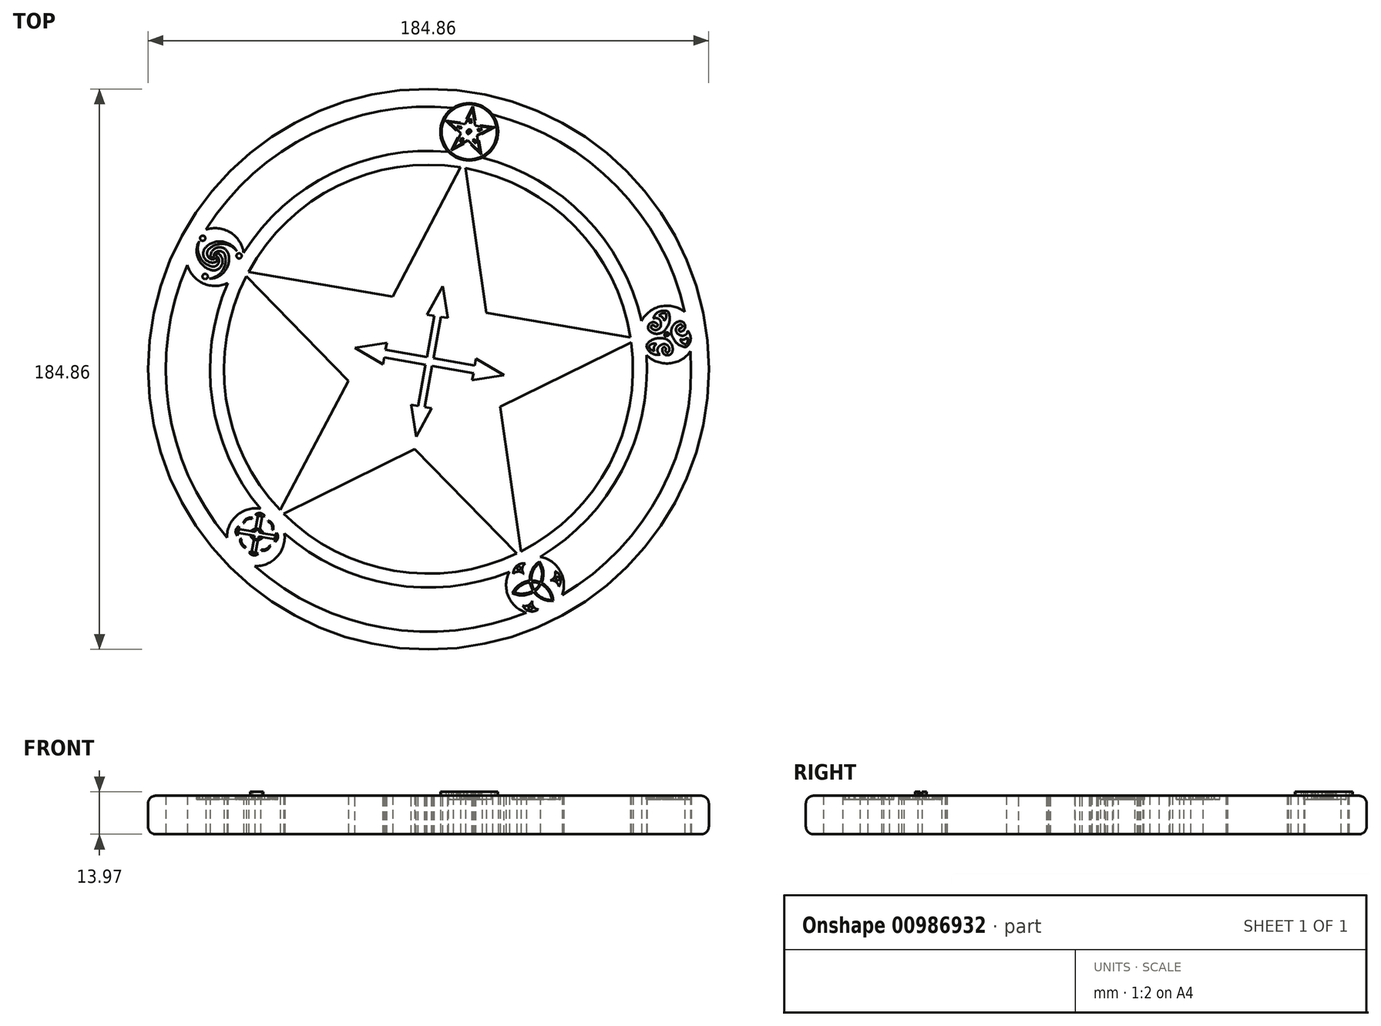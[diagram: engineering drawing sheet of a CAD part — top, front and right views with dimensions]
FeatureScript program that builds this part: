
annotation { "Feature Type Name" : "Feature", "Feature Type Description" : "" }
export const myFeature = defineFeature(function(context is Context, id is Id, definition is map)
    precondition{}
    {
        {
            var Q0;
            Q0=qCreatedBy(makeId("Top.planeOp"),FACE);
            var sketch = newSketch(context, id + "F0", { "sketchPlane" : qUnion([Q0])});
            skCircle(sketch, "E0.cCircle", {"center": v(-145.8, 0) * mm, "radius": 21.6 * mm, "construction": true});
            skLineSegment(sketch, "E0.0", {"start": v(-122.17, -12.44) * mm, "end": v(-150.33, -26.32) * mm});
            skLineSegment(sketch, "E0.1", {"start": v(-150.33, -26.32) * mm, "end": v(-172.24, -3.83) * mm});
            skLineSegment(sketch, "E0.2", {"start": v(-172.24, -3.83) * mm, "end": v(-157.62, 23.95) * mm});
            skLineSegment(sketch, "E0.3", {"start": v(-157.62, 23.95) * mm, "end": v(-126.68, 18.64) * mm});
            skLineSegment(sketch, "E0.4", {"start": v(-126.68, 18.64) * mm, "end": v(-122.17, -12.44) * mm});
            skPoint(sketch, "E0.0.midPoint", {"position": v(-136.25, -19.38) * mm});
            skLineSegment(sketch, "E1", {"start": v(-150.33, -26.32) * mm, "end": v(-195.9, -48.79) * mm});
            skLineSegment(sketch, "E2", {"start": v(-195.9, -48.79) * mm, "end": v(-172.24, -3.83) * mm});
            skLineSegment(sketch, "E3", {"start": v(-150.33, -26.32) * mm, "end": v(-114.88, -62.7) * mm});
            skLineSegment(sketch, "E4", {"start": v(-114.88, -62.7) * mm, "end": v(-122.17, -12.44) * mm});
            skLineSegment(sketch, "E5", {"start": v(-122.17, -12.44) * mm, "end": v(-76.61, 10.03) * mm});
            skLineSegment(sketch, "E6", {"start": v(-76.61, 10.03) * mm, "end": v(-126.68, 18.64) * mm});
            skLineSegment(sketch, "E7", {"start": v(-126.68, 18.64) * mm, "end": v(-133.97, 68.91) * mm});
            skLineSegment(sketch, "E8", {"start": v(-133.97, 68.91) * mm, "end": v(-157.62, 23.95) * mm});
            skLineSegment(sketch, "E9", {"start": v(-157.62, 23.95) * mm, "end": v(-207.69, 32.56) * mm});
            skLineSegment(sketch, "E10", {"start": v(-207.69, 32.56) * mm, "end": v(-172.24, -3.83) * mm});
            skCircle(sketch, "E11", {"center": v(-145.8, 0) * mm, "radius": 69.92 * mm});
            skCircle(sketch, "E12", {"center": v(-132.35, 78.3) * mm, "radius": 9.53 * mm});
            skCircle(sketch, "E13", {"center": v(-67.18, 11.4) * mm, "radius": 9.53 * mm});
            skCircle(sketch, "E14", {"center": v(-110.67, -71.25) * mm, "radius": 9.53 * mm});
            skCircle(sketch, "E15", {"center": v(-202.71, -55.44) * mm, "radius": 9.53 * mm});
            skCircle(sketch, "E16", {"center": v(-216.12, 37) * mm, "radius": 9.53 * mm});
            skCircle(sketch, "E17", {"center": v(-145.8, 0) * mm, "radius": 88.97 * mm});
            skCircle(sketch, "E18", {"center": v(-145.8, 0) * mm, "radius": 67.43 * mm});
            skCircle(sketch, "E19", {"center": v(-145.8, 0) * mm, "radius": 92.43 * mm});
            skCircle(sketch, "E20", {"center": v(-145.8, 0) * mm, "radius": 72.01 * mm});
            skCircle(sketch, "E21", {"center": v(-145.8, 0) * mm, "radius": 86.59 * mm});
            skSolve(sketch);
        }
        {
            var Q0;
            Q0 = qSketchRegion(id + "F0", true);
            var Q1;
            {var subQ0=sQuery(id+"F0.wireOp",EDGE,"E0.3");Q1=makeQuery(id+"F0.imprint","IMPRINT",FACE,{"disambiguationData":[TD([[makeQuery(id+"F0.imprint","IMPRINT",EDGE,{"derivedFrom":subQ0}),1.0]])]});}
            var Q2;
            Q2=makeQuery(id+"F0.imprint","IMPRINT",FACE,{"disambiguationData":[TD([[makeQuery(id+"F0.imprint","IMPRINT",EDGE,{"derivedFrom":sQuery(id+"F0.wireOp",EDGE,"E0.0")}),-1.0]])]});
            var Q3;
            {var subQ0=sQuery(id+"F0.wireOp",EDGE,"E0.2");Q3=makeQuery(id+"F0.imprint","IMPRINT",FACE,{"disambiguationData":[TD([[makeQuery(id+"F0.imprint","IMPRINT",EDGE,{"derivedFrom":subQ0}),1.0]])]});}
            var Q4;
            {var subQ0=sQuery(id+"F0.wireOp",EDGE,"E0.4");Q4=makeQuery(id+"F0.imprint","IMPRINT",FACE,{"disambiguationData":[TD([[makeQuery(id+"F0.imprint","IMPRINT",EDGE,{"derivedFrom":subQ0}),1.0]])]});}
            var Q5;
            {var subQ0=sQuery(id+"F0.wireOp",EDGE,"E0.0");Q5=makeQuery(id+"F0.imprint","IMPRINT",FACE,{"disambiguationData":[TD([[makeQuery(id+"F0.imprint","IMPRINT",EDGE,{"derivedFrom":subQ0}),1.0]])]});}
            var Q6;
            {var subQ1=sQuery(id+"F0.wireOp",EDGE,"E8");var subQ3=sQuery(id+"F0.wireOp",EDGE,"E18");var subQ4=makeQuery(id+"F0.imprint","INTERSECT",VERTEX,{"derivedFrom":[subQ1,subQ3]});Q6=makeQuery(id+"F0.imprint","IMPRINT",FACE,{"disambiguationData":[TD([[makeQuery(id+"F0.imprint","IMPRINT",EDGE,{"disambiguationData":[TD([[subQ4,-1.0]])],"derivedFrom":subQ3}),-1.0]])]});}
            var Q7;
            {var subQ0=sQuery(id+"F0.wireOp",EDGE,"E12");var subQ5=sQuery(id+"F0.wireOp",EDGE,"E20");var subQ6=makeQuery(id+"F0.imprint","INTERSECT",VERTEX,{"disambiguationData":[OD(0.0)],"derivedFrom":[subQ0,subQ5]});Q7=makeQuery(id+"F0.imprint","IMPRINT",FACE,{"disambiguationData":[TD([[makeQuery(id+"F0.imprint","IMPRINT",EDGE,{"disambiguationData":[TD([[subQ6,-1.0]])],"derivedFrom":subQ5}),1.0]])]});}
            var Q8;
            {var subQ1=sQuery(id+"F0.wireOp",EDGE,"E9");var subQ3=sQuery(id+"F0.wireOp",EDGE,"E18");var subQ4=makeQuery(id+"F0.imprint","INTERSECT",VERTEX,{"derivedFrom":[subQ1,subQ3]});Q8=makeQuery(id+"F0.imprint","IMPRINT",FACE,{"disambiguationData":[TD([[makeQuery(id+"F0.imprint","IMPRINT",EDGE,{"disambiguationData":[TD([[subQ4,-1.0]])],"derivedFrom":subQ3}),-1.0]])]});}
            var Q9;
            {var subQ1=sQuery(id+"F0.wireOp",EDGE,"E2");var subQ3=sQuery(id+"F0.wireOp",EDGE,"E18");var subQ4=makeQuery(id+"F0.imprint","INTERSECT",VERTEX,{"derivedFrom":[subQ1,subQ3]});Q9=makeQuery(id+"F0.imprint","IMPRINT",FACE,{"disambiguationData":[TD([[makeQuery(id+"F0.imprint","IMPRINT",EDGE,{"disambiguationData":[TD([[subQ4,1.0]])],"derivedFrom":subQ3}),-1.0]])]});}
            var Q10;
            {var subQ0=sQuery(id+"F0.wireOp",EDGE,"E16");var subQ2=sQuery(id+"F0.wireOp",EDGE,"E20");var subQ4=makeQuery(id+"F0.imprint","INTERSECT",VERTEX,{"disambiguationData":[OD(0.0)],"derivedFrom":[subQ0,subQ2]});Q10=makeQuery(id+"F0.imprint","IMPRINT",FACE,{"disambiguationData":[TD([[makeQuery(id+"F0.imprint","IMPRINT",EDGE,{"disambiguationData":[TD([[subQ4,-1.0]])],"derivedFrom":subQ2}),1.0]])]});}
            var Q11;
            {var subQ0=sQuery(id+"F0.wireOp",EDGE,"E15");var subQ5=sQuery(id+"F0.wireOp",EDGE,"E20");var subQ6=makeQuery(id+"F0.imprint","INTERSECT",VERTEX,{"disambiguationData":[OD(1.0)],"derivedFrom":[subQ0,subQ5]});Q11=makeQuery(id+"F0.imprint","IMPRINT",FACE,{"disambiguationData":[TD([[makeQuery(id+"F0.imprint","IMPRINT",EDGE,{"disambiguationData":[TD([[subQ6,1.0]])],"derivedFrom":subQ5}),1.0]])]});}
            var Q12;
            {var subQ0=sQuery(id+"F0.wireOp",EDGE,"E21");var subQ1=sQuery(id+"F0.wireOp",EDGE,"E16");var subQ2=makeQuery(id+"F0.imprint","INTERSECT",VERTEX,{"disambiguationData":[OD(0.0)],"derivedFrom":[subQ1,subQ0]});Q12=makeQuery(id+"F0.imprint","IMPRINT",FACE,{"disambiguationData":[TD([[makeQuery(id+"F0.imprint","IMPRINT",EDGE,{"disambiguationData":[TD([[subQ2,1.0]])],"derivedFrom":subQ1}),1.0]])]});}
            var Q13;
            {var subQ0=sQuery(id+"F0.wireOp",EDGE,"E21");var subQ1=sQuery(id+"F0.wireOp",EDGE,"E16");var subQ2=makeQuery(id+"F0.imprint","INTERSECT",VERTEX,{"disambiguationData":[OD(0.0)],"derivedFrom":[subQ1,subQ0]});Q13=makeQuery(id+"F0.imprint","IMPRINT",FACE,{"disambiguationData":[TD([[makeQuery(id+"F0.imprint","IMPRINT",EDGE,{"disambiguationData":[TD([[subQ2,-1.0]])],"derivedFrom":subQ1}),1.0]])]});}
            var Q14;
            {var subQ0=sQuery(id+"F0.wireOp",EDGE,"E21");var subQ1=sQuery(id+"F0.wireOp",EDGE,"E15");var subQ2=makeQuery(id+"F0.imprint","INTERSECT",VERTEX,{"disambiguationData":[OD(0.0)],"derivedFrom":[subQ1,subQ0]});Q14=makeQuery(id+"F0.imprint","IMPRINT",FACE,{"disambiguationData":[TD([[makeQuery(id+"F0.imprint","IMPRINT",EDGE,{"disambiguationData":[TD([[subQ2,-1.0]])],"derivedFrom":subQ1}),-1.0]])]});}
            var Q15;
            {var subQ0=sQuery(id+"F0.wireOp",EDGE,"E0.1");Q15=makeQuery(id+"F0.imprint","IMPRINT",FACE,{"disambiguationData":[TD([[makeQuery(id+"F0.imprint","IMPRINT",EDGE,{"derivedFrom":subQ0}),1.0]])]});}
            var Q16;
            {var subQ1=sQuery(id+"F0.wireOp",EDGE,"E1");var subQ3=sQuery(id+"F0.wireOp",EDGE,"E18");var subQ4=makeQuery(id+"F0.imprint","INTERSECT",VERTEX,{"derivedFrom":[subQ1,subQ3]});Q16=makeQuery(id+"F0.imprint","IMPRINT",FACE,{"disambiguationData":[TD([[makeQuery(id+"F0.imprint","IMPRINT",EDGE,{"disambiguationData":[TD([[subQ4,1.0]])],"derivedFrom":subQ3}),-1.0]])]});}
            var Q17;
            {var subQ0=sQuery(id+"F0.wireOp",EDGE,"E15");var subQ2=sQuery(id+"F0.wireOp",EDGE,"E20");var subQ3=makeQuery(id+"F0.imprint","INTERSECT",VERTEX,{"disambiguationData":[OD(0.0)],"derivedFrom":[subQ0,subQ2]});Q17=makeQuery(id+"F0.imprint","IMPRINT",FACE,{"disambiguationData":[TD([[makeQuery(id+"F0.imprint","IMPRINT",EDGE,{"disambiguationData":[TD([[subQ3,1.0]])],"derivedFrom":subQ2}),1.0]])]});}
            var Q18;
            {var subQ0=sQuery(id+"F0.wireOp",EDGE,"E20");var subQ1=sQuery(id+"F0.wireOp",EDGE,"E15");var subQ2=makeQuery(id+"F0.imprint","INTERSECT",VERTEX,{"disambiguationData":[OD(1.0)],"derivedFrom":[subQ1,subQ0]});Q18=makeQuery(id+"F0.imprint","IMPRINT",FACE,{"disambiguationData":[TD([[makeQuery(id+"F0.imprint","IMPRINT",EDGE,{"disambiguationData":[TD([[subQ2,-1.0]])],"derivedFrom":subQ1}),1.0]])]});}
            var Q19;
            {var subQ0=sQuery(id+"F0.wireOp",EDGE,"E21");var subQ1=sQuery(id+"F0.wireOp",EDGE,"E15");var subQ2=makeQuery(id+"F0.imprint","INTERSECT",VERTEX,{"disambiguationData":[OD(0.0)],"derivedFrom":[subQ1,subQ0]});Q19=makeQuery(id+"F0.imprint","IMPRINT",FACE,{"disambiguationData":[TD([[makeQuery(id+"F0.imprint","IMPRINT",EDGE,{"disambiguationData":[TD([[subQ2,-1.0]])],"derivedFrom":subQ1}),1.0]])]});}
            var Q20;
            {var subQ1=sQuery(id+"F0.wireOp",EDGE,"E1");var subQ3=sQuery(id+"F0.wireOp",EDGE,"E18");var subQ4=makeQuery(id+"F0.imprint","INTERSECT",VERTEX,{"derivedFrom":[subQ1,subQ3]});Q20=makeQuery(id+"F0.imprint","IMPRINT",FACE,{"disambiguationData":[TD([[makeQuery(id+"F0.imprint","IMPRINT",EDGE,{"disambiguationData":[TD([[subQ4,-1.0]])],"derivedFrom":subQ3}),-1.0]])]});}
            var Q21;
            {var subQ3=sQuery(id+"F0.wireOp",EDGE,"E14");var subQ5=sQuery(id+"F0.wireOp",EDGE,"E20");var subQ6=makeQuery(id+"F0.imprint","INTERSECT",VERTEX,{"disambiguationData":[OD(1.0)],"derivedFrom":[subQ3,subQ5]});Q21=makeQuery(id+"F0.imprint","IMPRINT",FACE,{"disambiguationData":[TD([[makeQuery(id+"F0.imprint","IMPRINT",EDGE,{"disambiguationData":[TD([[subQ6,1.0]])],"derivedFrom":subQ5}),1.0]])]});}
            var Q22;
            {var subQ0=sQuery(id+"F0.wireOp",EDGE,"E21");var subQ1=sQuery(id+"F0.wireOp",EDGE,"E14");var subQ2=makeQuery(id+"F0.imprint","INTERSECT",VERTEX,{"disambiguationData":[OD(0.0)],"derivedFrom":[subQ1,subQ0]});Q22=makeQuery(id+"F0.imprint","IMPRINT",FACE,{"disambiguationData":[TD([[makeQuery(id+"F0.imprint","IMPRINT",EDGE,{"disambiguationData":[TD([[subQ2,-1.0]])],"derivedFrom":subQ1}),-1.0]])]});}
            var Q23;
            {var subQ1=sQuery(id+"F0.wireOp",EDGE,"E3");var subQ3=sQuery(id+"F0.wireOp",EDGE,"E18");var subQ4=makeQuery(id+"F0.imprint","INTERSECT",VERTEX,{"derivedFrom":[subQ1,subQ3]});Q23=makeQuery(id+"F0.imprint","IMPRINT",FACE,{"disambiguationData":[TD([[makeQuery(id+"F0.imprint","IMPRINT",EDGE,{"disambiguationData":[TD([[subQ4,-1.0]])],"derivedFrom":subQ3}),-1.0]])]});}
            var Q24;
            {var subQ0=sQuery(id+"F0.wireOp",EDGE,"E14");var subQ2=sQuery(id+"F0.wireOp",EDGE,"E20");var subQ3=makeQuery(id+"F0.imprint","INTERSECT",VERTEX,{"disambiguationData":[OD(0.0)],"derivedFrom":[subQ0,subQ2]});Q24=makeQuery(id+"F0.imprint","IMPRINT",FACE,{"disambiguationData":[TD([[makeQuery(id+"F0.imprint","IMPRINT",EDGE,{"disambiguationData":[TD([[subQ3,1.0]])],"derivedFrom":subQ2}),1.0]])]});}
            var Q25;
            {var subQ1=sQuery(id+"F0.wireOp",EDGE,"E4");var subQ3=sQuery(id+"F0.wireOp",EDGE,"E18");var subQ4=makeQuery(id+"F0.imprint","INTERSECT",VERTEX,{"derivedFrom":[subQ1,subQ3]});Q25=makeQuery(id+"F0.imprint","IMPRINT",FACE,{"disambiguationData":[TD([[makeQuery(id+"F0.imprint","IMPRINT",EDGE,{"disambiguationData":[TD([[subQ4,-1.0]])],"derivedFrom":subQ3}),-1.0]])]});}
            var Q26;
            {var subQ3=sQuery(id+"F0.wireOp",EDGE,"E13");var subQ5=sQuery(id+"F0.wireOp",EDGE,"E20");var subQ6=makeQuery(id+"F0.imprint","INTERSECT",VERTEX,{"disambiguationData":[OD(1.0)],"derivedFrom":[subQ3,subQ5]});Q26=makeQuery(id+"F0.imprint","IMPRINT",FACE,{"disambiguationData":[TD([[makeQuery(id+"F0.imprint","IMPRINT",EDGE,{"disambiguationData":[TD([[subQ6,1.0]])],"derivedFrom":subQ5}),1.0]])]});}
            var Q27;
            {var subQ0=sQuery(id+"F0.wireOp",EDGE,"E20");var subQ1=sQuery(id+"F0.wireOp",EDGE,"E14");var subQ2=makeQuery(id+"F0.imprint","INTERSECT",VERTEX,{"disambiguationData":[OD(1.0)],"derivedFrom":[subQ1,subQ0]});Q27=makeQuery(id+"F0.imprint","IMPRINT",FACE,{"disambiguationData":[TD([[makeQuery(id+"F0.imprint","IMPRINT",EDGE,{"disambiguationData":[TD([[subQ2,-1.0]])],"derivedFrom":subQ1}),1.0]])]});}
            var Q28;
            {var subQ0=sQuery(id+"F0.wireOp",EDGE,"E21");var subQ1=sQuery(id+"F0.wireOp",EDGE,"E14");var subQ2=makeQuery(id+"F0.imprint","INTERSECT",VERTEX,{"disambiguationData":[OD(0.0)],"derivedFrom":[subQ1,subQ0]});Q28=makeQuery(id+"F0.imprint","IMPRINT",FACE,{"disambiguationData":[TD([[makeQuery(id+"F0.imprint","IMPRINT",EDGE,{"disambiguationData":[TD([[subQ2,-1.0]])],"derivedFrom":subQ1}),1.0]])]});}
            var Q29;
            {var subQ0=sQuery(id+"F0.wireOp",EDGE,"E17");var subQ1=sQuery(id+"F0.wireOp",EDGE,"E13");var subQ2=makeQuery(id+"F0.imprint","INTERSECT",VERTEX,{"derivedFrom":[subQ1,subQ0]});Q29=makeQuery(id+"F0.imprint","IMPRINT",FACE,{"disambiguationData":[TD([[makeQuery(id+"F0.imprint","IMPRINT",EDGE,{"disambiguationData":[TD([[subQ2,1.0]])],"derivedFrom":subQ1}),-1.0]])]});}
            var Q30;
            {var subQ0=sQuery(id+"F0.wireOp",EDGE,"E13");var subQ2=sQuery(id+"F0.wireOp",EDGE,"E20");var subQ3=makeQuery(id+"F0.imprint","INTERSECT",VERTEX,{"disambiguationData":[OD(0.0)],"derivedFrom":[subQ0,subQ2]});Q30=makeQuery(id+"F0.imprint","IMPRINT",FACE,{"disambiguationData":[TD([[makeQuery(id+"F0.imprint","IMPRINT",EDGE,{"disambiguationData":[TD([[subQ3,1.0]])],"derivedFrom":subQ2}),1.0]])]});}
            var Q31;
            {var subQ1=sQuery(id+"F0.wireOp",EDGE,"E5");var subQ3=sQuery(id+"F0.wireOp",EDGE,"E18");var subQ4=makeQuery(id+"F0.imprint","INTERSECT",VERTEX,{"derivedFrom":[subQ1,subQ3]});Q31=makeQuery(id+"F0.imprint","IMPRINT",FACE,{"disambiguationData":[TD([[makeQuery(id+"F0.imprint","IMPRINT",EDGE,{"disambiguationData":[TD([[subQ4,-1.0]])],"derivedFrom":subQ3}),-1.0]])]});}
            var Q32;
            {var subQ1=sQuery(id+"F0.wireOp",EDGE,"E6");var subQ3=sQuery(id+"F0.wireOp",EDGE,"E18");var subQ4=makeQuery(id+"F0.imprint","INTERSECT",VERTEX,{"derivedFrom":[subQ1,subQ3]});Q32=makeQuery(id+"F0.imprint","IMPRINT",FACE,{"disambiguationData":[TD([[makeQuery(id+"F0.imprint","IMPRINT",EDGE,{"disambiguationData":[TD([[subQ4,-1.0]])],"derivedFrom":subQ3}),-1.0]])]});}
            var Q33;
            {var subQ3=sQuery(id+"F0.wireOp",EDGE,"E12");var subQ5=sQuery(id+"F0.wireOp",EDGE,"E20");var subQ6=makeQuery(id+"F0.imprint","INTERSECT",VERTEX,{"disambiguationData":[OD(1.0)],"derivedFrom":[subQ3,subQ5]});Q33=makeQuery(id+"F0.imprint","IMPRINT",FACE,{"disambiguationData":[TD([[makeQuery(id+"F0.imprint","IMPRINT",EDGE,{"disambiguationData":[TD([[subQ6,1.0]])],"derivedFrom":subQ5}),1.0]])]});}
            var Q34;
            {var subQ0=sQuery(id+"F0.wireOp",EDGE,"E21");var subQ1=sQuery(id+"F0.wireOp",EDGE,"E13");var subQ2=makeQuery(id+"F0.imprint","INTERSECT",VERTEX,{"disambiguationData":[OD(0.0)],"derivedFrom":[subQ1,subQ0]});Q34=makeQuery(id+"F0.imprint","IMPRINT",FACE,{"disambiguationData":[TD([[makeQuery(id+"F0.imprint","IMPRINT",EDGE,{"disambiguationData":[TD([[subQ2,-1.0]])],"derivedFrom":subQ1}),1.0]])]});}
            var Q35;
            {var subQ0=sQuery(id+"F0.wireOp",EDGE,"E21");var subQ1=sQuery(id+"F0.wireOp",EDGE,"E13");var subQ2=makeQuery(id+"F0.imprint","INTERSECT",VERTEX,{"disambiguationData":[OD(0.0)],"derivedFrom":[subQ1,subQ0]});Q35=makeQuery(id+"F0.imprint","IMPRINT",FACE,{"disambiguationData":[TD([[makeQuery(id+"F0.imprint","IMPRINT",EDGE,{"disambiguationData":[TD([[subQ2,1.0]])],"derivedFrom":subQ1}),1.0]])]});}
            var Q36;
            {var subQ0=sQuery(id+"F0.wireOp",EDGE,"E17");var subQ1=sQuery(id+"F0.wireOp",EDGE,"E12");var subQ2=makeQuery(id+"F0.imprint","INTERSECT",VERTEX,{"derivedFrom":[subQ1,subQ0]});Q36=makeQuery(id+"F0.imprint","IMPRINT",FACE,{"disambiguationData":[TD([[makeQuery(id+"F0.imprint","IMPRINT",EDGE,{"disambiguationData":[TD([[subQ2,1.0]])],"derivedFrom":subQ1}),-1.0]])]});}
            var Q37;
            {var subQ0=sQuery(id+"F0.wireOp",EDGE,"E17");var subQ1=sQuery(id+"F0.wireOp",EDGE,"E12");var subQ2=makeQuery(id+"F0.imprint","INTERSECT",VERTEX,{"derivedFrom":[subQ1,subQ0]});Q37=makeQuery(id+"F0.imprint","IMPRINT",FACE,{"disambiguationData":[TD([[makeQuery(id+"F0.imprint","IMPRINT",EDGE,{"disambiguationData":[TD([[subQ2,-1.0]])],"derivedFrom":subQ1}),-1.0]])]});}
            var Q38;
            {var subQ0=sQuery(id+"F0.wireOp",EDGE,"E12");var subQ1=makeQuery(id+"F0.imprint","INTERSECT",VERTEX,{"derivedFrom":[subQ0,sQuery(id+"F0.wireOp",EDGE,"E17")]});Q38=makeQuery(id+"F0.imprint","IMPRINT",FACE,{"disambiguationData":[TD([[makeQuery(id+"F0.imprint","IMPRINT",EDGE,{"disambiguationData":[TD([[subQ1,1.0]])],"derivedFrom":subQ0}),1.0]])]});}
            var Q39;
            {var subQ0=sQuery(id+"F0.wireOp",EDGE,"E21");var subQ1=sQuery(id+"F0.wireOp",EDGE,"E12");var subQ2=makeQuery(id+"F0.imprint","INTERSECT",VERTEX,{"disambiguationData":[OD(1.0)],"derivedFrom":[subQ1,subQ0]});Q39=makeQuery(id+"F0.imprint","IMPRINT",FACE,{"disambiguationData":[TD([[makeQuery(id+"F0.imprint","IMPRINT",EDGE,{"disambiguationData":[TD([[subQ2,-1.0]])],"derivedFrom":subQ1}),1.0]])]});}
            var Q40;
            {var subQ0=sQuery(id+"F0.wireOp",EDGE,"E12");var subQ2=sQuery(id+"F0.wireOp",EDGE,"E20");var subQ3=makeQuery(id+"F0.imprint","INTERSECT",VERTEX,{"disambiguationData":[OD(0.0)],"derivedFrom":[subQ0,subQ2]});Q40=makeQuery(id+"F0.imprint","IMPRINT",FACE,{"disambiguationData":[TD([[makeQuery(id+"F0.imprint","IMPRINT",EDGE,{"disambiguationData":[TD([[subQ3,1.0]])],"derivedFrom":subQ2}),1.0]])]});}
            var Q41;
            {var subQ1=sQuery(id+"F0.wireOp",EDGE,"E7");var subQ3=sQuery(id+"F0.wireOp",EDGE,"E18");var subQ4=makeQuery(id+"F0.imprint","INTERSECT",VERTEX,{"derivedFrom":[subQ1,subQ3]});Q41=makeQuery(id+"F0.imprint","IMPRINT",FACE,{"disambiguationData":[TD([[makeQuery(id+"F0.imprint","IMPRINT",EDGE,{"disambiguationData":[TD([[subQ4,-1.0]])],"derivedFrom":subQ3}),-1.0]])]});}
            extrude(context, id + "F1", {"entities" : qUnion([Q0, Q1, Q2, Q3, Q4, Q5, Q6, Q7, Q8, Q9, Q10, Q11, Q12, Q13, Q14, Q15, Q16, Q17, Q18, Q19, Q20, Q21, Q22, Q23, Q24, Q25, Q26, Q27, Q28, Q29, Q30, Q31, Q32, Q33, Q34, Q35, Q36, Q37, Q38, Q39, Q40, Q41]), "depth" : 12.7 * mm, "offsetDistance" : 25.4 * mm});
        }
        {
            var Q0;
            Q0=makeQuery(id+"F1.opExtrude","CAP_EDGE",EDGE,{"disambiguationData":[OSD([sQuery(id+"F0.wireOp",EDGE,"E19")])],"isStart":false});
            var Q1;
            Q1=makeQuery(id+"F1.opExtrude","CAP_EDGE",EDGE,{"disambiguationData":[OSD([sQuery(id+"F0.wireOp",EDGE,"E19")])],"isStart":true});
            fillet(context, id + "F2", {"entities" : qUnion([Q0, Q1]), "radius" : 2.54 * mm, "tangentPropagation" : true, "allowEdgeOverflow" : false});
        }
        {
            var Q0;
            Q0=makeQuery(id+"F1.opExtrude","CAP_FACE",FACE,{"disambiguationData":[OSD([sQuery(id+"F0.wireOp",EDGE,"E1"),sQuery(id+"F0.wireOp",EDGE,"E2"),sQuery(id+"F0.wireOp",EDGE,"E3"),sQuery(id+"F0.wireOp",EDGE,"E4"),sQuery(id+"F0.wireOp",EDGE,"E5"),sQuery(id+"F0.wireOp",EDGE,"E6"),sQuery(id+"F0.wireOp",EDGE,"E7"),sQuery(id+"F0.wireOp",EDGE,"E8"),sQuery(id+"F0.wireOp",EDGE,"E9"),sQuery(id+"F0.wireOp",EDGE,"E10"),sQuery(id+"F0.wireOp",EDGE,"E12"),sQuery(id+"F0.wireOp",EDGE,"E13"),sQuery(id+"F0.wireOp",EDGE,"E14"),sQuery(id+"F0.wireOp",EDGE,"E15"),sQuery(id+"F0.wireOp",EDGE,"E16"),sQuery(id+"F0.wireOp",EDGE,"E18"),sQuery(id+"F0.wireOp",EDGE,"E19"),sQuery(id+"F0.wireOp",EDGE,"E20"),sQuery(id+"F0.wireOp",EDGE,"E21")])],"isStart":false});
            var sketch = newSketch(context, id + "F3", { "sketchPlane" : qUnion([Q0])});
            skCircle(sketch, "E22", {"center": v(-220.21, 43.2) * mm, "radius": 0.86 * mm});
            skCircle(sketch, "E23", {"center": v(-219.42, 30.57) * mm, "radius": 0.86 * mm});
            skCircle(sketch, "E24", {"center": v(-208.22, 37.38) * mm, "radius": 0.86 * mm});
            skCircle(sketch, "E25", {"center": v(-216.12, 37) * mm, "radius": 0.48 * mm});
            skArc(sketch, "E26", {"start": v(-211.67, 37.67) * mm, "mid": v(-214.6, 40.21) * mm, "end": v(-217.59, 37.75) * mm});
            skArc(sketch, "E27", {"start": v(-218.08, 29.83) * mm, "mid": v(-213.02, 32.24) * mm, "end": v(-211.67, 37.67) * mm});
            skArc(sketch, "E28", {"start": v(-218.08, 29.83) * mm, "mid": v(-213.79, 32.38) * mm, "end": v(-212.77, 37.26) * mm});
            skCircle(sketch, "E29", {"center": v(-217.08, 37.47) * mm, "radius": 0.59 * mm});
            skArc(sketch, "E30", {"start": v(-212.77, 37.26) * mm, "mid": v(-214.48, 38.95) * mm, "end": v(-216.57, 37.76) * mm});
            skCircle(sketch, "E31.1.0", {"center": v(-215.22, 37.58) * mm, "radius": 0.59 * mm});
            skArc(sketch, "E31.1.1", {"start": v(-217.55, 33.96) * mm, "mid": v(-215.24, 34.6) * mm, "end": v(-215.22, 37) * mm});
            skArc(sketch, "E31.1.2", {"start": v(-217.75, 32.8) * mm, "mid": v(-214.09, 34.06) * mm, "end": v(-214.72, 37.88) * mm});
            skArc(sketch, "E31.1.4", {"start": v(-221.33, 42.27) * mm, "mid": v(-221.77, 36.69) * mm, "end": v(-217.75, 32.8) * mm});
            skArc(sketch, "E31.1.5", {"start": v(-221.33, 42.27) * mm, "mid": v(-221.27, 37.28) * mm, "end": v(-217.55, 33.96) * mm});
            skCircle(sketch, "E31.2.0", {"center": v(-216.05, 35.92) * mm, "radius": 0.59 * mm});
            skArc(sketch, "E31.2.1", {"start": v(-218.02, 39.75) * mm, "mid": v(-218.63, 37.43) * mm, "end": v(-216.56, 36.21) * mm});
            skArc(sketch, "E31.2.2", {"start": v(-218.93, 40.5) * mm, "mid": v(-219.67, 36.7) * mm, "end": v(-216.04, 35.33) * mm});
            skArc(sketch, "E31.2.4", {"start": v(-208.94, 38.87) * mm, "mid": v(-213.55, 42.04) * mm, "end": v(-218.93, 40.5) * mm});
            skArc(sketch, "E31.2.5", {"start": v(-208.94, 38.87) * mm, "mid": v(-213.29, 41.31) * mm, "end": v(-218.02, 39.75) * mm});
            skLineSegment(sketch, "E31.anchor1", {"start": v(-216.12, 37) * mm, "end": v(-217.59, 37.75) * mm, "construction": true});
            skLineSegment(sketch, "E31.anchor2", {"start": v(-216.12, 37) * mm, "end": v(-216.04, 35.33) * mm, "construction": true});
            skLineSegment(sketch, "E32", {"start": v(-202, -48.43) * mm, "end": v(-202.91, -53.65) * mm});
            skLineSegment(sketch, "E33", {"start": v(-200.67, -48.67) * mm, "end": v(-201.59, -53.88) * mm});
            skLineSegment(sketch, "E34", {"start": v(-202, -48.43) * mm, "end": v(-202.82, -47.9) * mm});
            skLineSegment(sketch, "E35", {"start": v(-200.67, -48.67) * mm, "end": v(-199.8, -48.44) * mm});
            skArc(sketch, "E36", {"start": v(-199.8, -48.44) * mm, "mid": v(-201.18, -47.46) * mm, "end": v(-202.82, -47.9) * mm});
            skLineSegment(sketch, "E37", {"start": v(-201.42, -48.65) * mm, "end": v(-200.65, -48.15) * mm});
            skLineSegment(sketch, "E38", {"start": v(-201.42, -48.65) * mm, "end": v(-201.93, -47.88) * mm});
            skArc(sketch, "E39", {"start": v(-200.65, -48.15) * mm, "mid": v(-201.24, -47.79) * mm, "end": v(-201.93, -47.88) * mm});
            skLineSegment(sketch, "E40.1.0", {"start": v(-208.36, -54.06) * mm, "end": v(-203.14, -54.98) * mm});
            skArc(sketch, "E40.1.1", {"start": v(-208.35, -51.85) * mm, "mid": v(-209.33, -53.24) * mm, "end": v(-208.89, -54.88) * mm});
            skLineSegment(sketch, "E40.1.2", {"start": v(-208.36, -54.06) * mm, "end": v(-208.89, -54.88) * mm});
            skArc(sketch, "E40.1.3", {"start": v(-208.65, -52.71) * mm, "mid": v(-209, -53.3) * mm, "end": v(-208.91, -53.99) * mm});
            skLineSegment(sketch, "E40.1.4", {"start": v(-208.13, -52.73) * mm, "end": v(-202.91, -53.65) * mm});
            skLineSegment(sketch, "E40.1.5", {"start": v(-208.14, -53.48) * mm, "end": v(-208.65, -52.71) * mm});
            skLineSegment(sketch, "E40.1.6", {"start": v(-208.14, -53.48) * mm, "end": v(-208.91, -53.99) * mm});
            skLineSegment(sketch, "E40.1.7", {"start": v(-208.13, -52.73) * mm, "end": v(-208.35, -51.85) * mm});
            skLineSegment(sketch, "E40.2.0", {"start": v(-202.74, -60.42) * mm, "end": v(-201.82, -55.2) * mm});
            skArc(sketch, "E40.2.1", {"start": v(-204.94, -60.41) * mm, "mid": v(-203.55, -61.39) * mm, "end": v(-201.91, -60.95) * mm});
            skLineSegment(sketch, "E40.2.2", {"start": v(-202.74, -60.42) * mm, "end": v(-201.91, -60.95) * mm});
            skArc(sketch, "E40.2.3", {"start": v(-204.08, -60.7) * mm, "mid": v(-203.49, -61.07) * mm, "end": v(-202.8, -60.97) * mm});
            skLineSegment(sketch, "E40.2.4", {"start": v(-204.07, -60.19) * mm, "end": v(-203.15, -54.97) * mm});
            skLineSegment(sketch, "E40.2.5", {"start": v(-203.31, -60.2) * mm, "end": v(-204.08, -60.7) * mm});
            skLineSegment(sketch, "E40.2.6", {"start": v(-203.31, -60.2) * mm, "end": v(-202.8, -60.97) * mm});
            skLineSegment(sketch, "E40.2.7", {"start": v(-204.07, -60.19) * mm, "end": v(-204.94, -60.41) * mm});
            skLineSegment(sketch, "E40.3.0", {"start": v(-196.37, -54.8) * mm, "end": v(-201.59, -53.88) * mm});
            skArc(sketch, "E40.3.1", {"start": v(-196.38, -57) * mm, "mid": v(-195.4, -55.61) * mm, "end": v(-195.85, -53.97) * mm});
            skLineSegment(sketch, "E40.3.2", {"start": v(-196.37, -54.8) * mm, "end": v(-195.85, -53.97) * mm});
            skArc(sketch, "E40.3.3", {"start": v(-196.09, -56.14) * mm, "mid": v(-195.73, -55.55) * mm, "end": v(-195.82, -54.86) * mm});
            skLineSegment(sketch, "E40.3.4", {"start": v(-196.6, -56.13) * mm, "end": v(-201.82, -55.2) * mm});
            skLineSegment(sketch, "E40.3.5", {"start": v(-196.6, -55.37) * mm, "end": v(-196.09, -56.14) * mm});
            skLineSegment(sketch, "E40.3.6", {"start": v(-196.6, -55.37) * mm, "end": v(-195.82, -54.86) * mm});
            skLineSegment(sketch, "E40.3.7", {"start": v(-196.6, -56.13) * mm, "end": v(-196.38, -57) * mm});
            skPoint(sketch, "E40.center", {"position": v(-202.37, -54.43) * mm});
            skArc(sketch, "E41", {"start": v(-203.83, -49.03) * mm, "mid": v(-205.67, -49.26) * mm, "end": v(-206.84, -50.68) * mm});
            skArc(sketch, "E42", {"start": v(-203.9, -49.4) * mm, "mid": v(-205.47, -49.56) * mm, "end": v(-206.54, -50.74) * mm});
            skLineSegment(sketch, "E43", {"start": v(-203.83, -49.03) * mm, "end": v(-203.9, -49.4) * mm});
            skLineSegment(sketch, "E44", {"start": v(-206.84, -50.68) * mm, "end": v(-206.54, -50.74) * mm});
            skArc(sketch, "E45.1.0", {"start": v(-207.76, -55.89) * mm, "mid": v(-207.54, -57.73) * mm, "end": v(-206.11, -58.9) * mm});
            skArc(sketch, "E45.1.1", {"start": v(-207.4, -55.95) * mm, "mid": v(-207.24, -57.53) * mm, "end": v(-206.06, -58.6) * mm});
            skLineSegment(sketch, "E45.1.2", {"start": v(-207.76, -55.89) * mm, "end": v(-207.4, -55.95) * mm});
            skLineSegment(sketch, "E45.1.3", {"start": v(-206.11, -58.9) * mm, "end": v(-206.06, -58.6) * mm});
            skArc(sketch, "E45.2.0", {"start": v(-200.9, -59.82) * mm, "mid": v(-199.07, -59.6) * mm, "end": v(-197.89, -58.17) * mm});
            skArc(sketch, "E45.2.1", {"start": v(-200.84, -59.46) * mm, "mid": v(-199.26, -59.3) * mm, "end": v(-198.2, -58.12) * mm});
            skLineSegment(sketch, "E45.2.2", {"start": v(-200.9, -59.82) * mm, "end": v(-200.84, -59.46) * mm});
            skLineSegment(sketch, "E45.2.3", {"start": v(-197.89, -58.17) * mm, "end": v(-198.2, -58.12) * mm});
            skArc(sketch, "E45.3.0", {"start": v(-196.97, -52.97) * mm, "mid": v(-197.2, -51.13) * mm, "end": v(-198.62, -49.95) * mm});
            skArc(sketch, "E45.3.1", {"start": v(-197.34, -52.9) * mm, "mid": v(-197.5, -51.32) * mm, "end": v(-198.68, -50.26) * mm});
            skLineSegment(sketch, "E45.3.2", {"start": v(-196.97, -52.97) * mm, "end": v(-197.34, -52.9) * mm});
            skLineSegment(sketch, "E45.3.3", {"start": v(-198.62, -49.95) * mm, "end": v(-198.68, -50.26) * mm});
            skArc(sketch, "E46", {"start": v(-200.67, -54.04) * mm, "mid": v(-202.1, -52.98) * mm, "end": v(-203.82, -53.49) * mm});
            skArc(sketch, "E47", {"start": v(-200.2, -54.12) * mm, "mid": v(-202.05, -52.68) * mm, "end": v(-204.3, -53.4) * mm});
            skArc(sketch, "E48", {"start": v(-204.05, -54.82) * mm, "mid": v(-202.64, -56.02) * mm, "end": v(-200.9, -55.37) * mm});
            skArc(sketch, "E49", {"start": v(-204.52, -54.73) * mm, "mid": v(-202.7, -56.38) * mm, "end": v(-200.44, -55.45) * mm});
            skArc(sketch, "E50", {"start": v(-104.64, -76.43) * mm, "mid": v(-110.4, -69.87) * mm, "end": v(-118.17, -73.88) * mm});
            skArc(sketch, "E51.1.0", {"start": v(-109.2, -63.44) * mm, "mid": v(-112, -71.72) * mm, "end": v(-104.64, -76.43) * mm});
            skArc(sketch, "E51.2.0", {"start": v(-118.17, -73.88) * mm, "mid": v(-109.6, -72.17) * mm, "end": v(-109.2, -63.44) * mm});
            skPoint(sketch, "E51.center", {"position": v(-110.67, -71.25) * mm});
            skLineSegment(sketch, "E52.0", {"start": v(-203.83, -49.03) * mm, "end": v(-201.53, -49.44) * mm, "construction": true});
            skLineSegment(sketch, "E53.0", {"start": v(-206.84, -50.68) * mm, "end": v(-206.54, -50.74) * mm, "construction": true});
            skLineSegment(sketch, "E54.0", {"start": v(-202.82, -47.9) * mm, "end": v(-199.8, -48.44) * mm, "construction": true});
            skLineSegment(sketch, "E55.0", {"start": v(-202, -48.43) * mm, "end": v(-200.67, -48.67) * mm, "construction": true});
            skLineSegment(sketch, "E56.0", {"start": v(-202.91, -53.65) * mm, "end": v(-201.59, -53.88) * mm, "construction": true});
            skLineSegment(sketch, "E57.0", {"start": v(-200.44, -55.45) * mm, "end": v(-200.2, -54.12) * mm, "construction": true});
            skLineSegment(sketch, "E58.0", {"start": v(-204.52, -54.73) * mm, "end": v(-204.3, -53.4) * mm, "construction": true});
            skLineSegment(sketch, "E59.0", {"start": v(-200.9, -55.37) * mm, "end": v(-200.67, -54.04) * mm, "construction": true});
            skLineSegment(sketch, "E60.0", {"start": v(-203.9, -49.4) * mm, "end": v(-203.83, -49.03) * mm, "construction": true});
            skLineSegment(sketch, "E61.0", {"start": v(-207.36, -53.6) * mm, "end": v(-206.84, -50.68) * mm, "construction": true});
            skLineSegment(sketch, "E62.0", {"start": v(-204.05, -54.82) * mm, "end": v(-203.82, -53.49) * mm, "construction": true});
            skArc(sketch, "E63", {"start": v(-113.85, -64.06) * mm, "mid": v(-116.65, -64.89) * mm, "end": v(-117.86, -67.54) * mm});
            skArc(sketch, "E64", {"start": v(-113.85, -64.06) * mm, "mid": v(-114.85, -65.7) * mm, "end": v(-114.34, -67.55) * mm});
            skArc(sketch, "E65", {"start": v(-114.34, -67.55) * mm, "mid": v(-116.1, -66.78) * mm, "end": v(-117.86, -67.54) * mm});
            skCircle(sketch, "E66", {"center": v(-116.02, -65.63) * mm, "radius": 0.58 * mm});
            skArc(sketch, "E67.1.0", {"start": v(-102.82, -71.75) * mm, "mid": v(-102.26, -68.89) * mm, "end": v(-104.06, -66.59) * mm});
            skArc(sketch, "E67.1.1", {"start": v(-102.82, -71.75) * mm, "mid": v(-103.81, -70.11) * mm, "end": v(-105.7, -69.7) * mm});
            skCircle(sketch, "E67.1.2", {"center": v(-103.21, -69.1) * mm, "radius": 0.58 * mm});
            skArc(sketch, "E67.1.3", {"start": v(-105.7, -69.7) * mm, "mid": v(-104.2, -68.5) * mm, "end": v(-104.06, -66.59) * mm});
            skArc(sketch, "E67.2.0", {"start": v(-114.74, -77.98) * mm, "mid": v(-112.45, -79.8) * mm, "end": v(-109.58, -79.27) * mm});
            skArc(sketch, "E67.2.1", {"start": v(-114.74, -77.98) * mm, "mid": v(-112.82, -77.86) * mm, "end": v(-111.6, -76.38) * mm});
            skCircle(sketch, "E67.2.2", {"center": v(-112.2, -78.86) * mm, "radius": 0.58 * mm});
            skArc(sketch, "E67.2.3", {"start": v(-111.6, -76.38) * mm, "mid": v(-111.22, -78.26) * mm, "end": v(-109.58, -79.27) * mm});
            skLineSegment(sketch, "E68.0", {"start": v(-129.8, 77.05) * mm, "end": v(-132.75, 75.48) * mm});
            skLineSegment(sketch, "E68.1", {"start": v(-132.75, 75.48) * mm, "end": v(-135.15, 77.8) * mm});
            skLineSegment(sketch, "E68.2", {"start": v(-135.15, 77.8) * mm, "end": v(-133.69, 80.8) * mm});
            skLineSegment(sketch, "E68.3", {"start": v(-133.69, 80.8) * mm, "end": v(-130.38, 80.34) * mm});
            skLineSegment(sketch, "E68.4", {"start": v(-130.38, 80.34) * mm, "end": v(-129.8, 77.05) * mm});
            skPoint(sketch, "E68.0.midPoint", {"position": v(-131.27, 76.27) * mm});
            skCircle(sketch, "E69", {"center": v(-132.35, 78.3) * mm, "radius": 9.5 * mm});
            skCircle(sketch, "E70", {"center": v(-132.35, 78.3) * mm, "radius": 9.1 * mm});
            skLineSegment(sketch, "E71", {"start": v(-135.15, 77.8) * mm, "end": v(-137.53, 72.94) * mm});
            skLineSegment(sketch, "E72", {"start": v(-137.53, 72.94) * mm, "end": v(-132.75, 75.48) * mm});
            skLineSegment(sketch, "E73", {"start": v(-132.75, 75.48) * mm, "end": v(-128.86, 71.72) * mm});
            skLineSegment(sketch, "E74", {"start": v(-128.86, 71.72) * mm, "end": v(-129.8, 77.05) * mm});
            skLineSegment(sketch, "E75", {"start": v(-129.8, 77.05) * mm, "end": v(-125.02, 79.6) * mm});
            skLineSegment(sketch, "E76", {"start": v(-125.02, 79.6) * mm, "end": v(-130.38, 80.34) * mm});
            skLineSegment(sketch, "E77", {"start": v(-130.38, 80.34) * mm, "end": v(-131.32, 85.67) * mm});
            skLineSegment(sketch, "E78", {"start": v(-131.32, 85.67) * mm, "end": v(-133.69, 80.8) * mm});
            skLineSegment(sketch, "E79", {"start": v(-133.69, 80.8) * mm, "end": v(-139.05, 81.56) * mm});
            skLineSegment(sketch, "E80", {"start": v(-139.05, 81.56) * mm, "end": v(-135.15, 77.8) * mm});
            skLineSegment(sketch, "E81.0", {"start": v(-130.38, 80.34) * mm, "end": v(-131.32, 85.67) * mm, "construction": true});
            skLineSegment(sketch, "E82", {"start": v(-132.47, 81.33) * mm, "end": v(-131.5, 81.2) * mm});
            skLineSegment(sketch, "E83", {"start": v(-131.5, 81.2) * mm, "end": v(-131.78, 82.75) * mm});
            skLineSegment(sketch, "E84", {"start": v(-131.78, 82.75) * mm, "end": v(-132.47, 81.33) * mm});
            skLineSegment(sketch, "E85.1.0", {"start": v(-134.85, 80) * mm, "end": v(-136.41, 80.22) * mm});
            skLineSegment(sketch, "E85.1.1", {"start": v(-136.41, 80.22) * mm, "end": v(-135.28, 79.12) * mm});
            skLineSegment(sketch, "E85.1.2", {"start": v(-135.28, 79.12) * mm, "end": v(-134.85, 80) * mm});
            skLineSegment(sketch, "E85.2.0", {"start": v(-134.75, 76.45) * mm, "end": v(-135.44, 75.03) * mm});
            skLineSegment(sketch, "E85.2.1", {"start": v(-135.44, 75.03) * mm, "end": v(-134.04, 75.77) * mm});
            skLineSegment(sketch, "E85.2.2", {"start": v(-134.04, 75.77) * mm, "end": v(-134.75, 76.45) * mm});
            skLineSegment(sketch, "E85.3.0", {"start": v(-131.34, 75.45) * mm, "end": v(-130.2, 74.35) * mm});
            skLineSegment(sketch, "E85.3.1", {"start": v(-130.2, 74.35) * mm, "end": v(-130.48, 75.91) * mm});
            skLineSegment(sketch, "E85.3.2", {"start": v(-130.48, 75.91) * mm, "end": v(-131.34, 75.45) * mm});
            skLineSegment(sketch, "E85.4.0", {"start": v(-129.33, 78.38) * mm, "end": v(-127.94, 79.13) * mm});
            skLineSegment(sketch, "E85.4.1", {"start": v(-127.94, 79.13) * mm, "end": v(-129.5, 79.35) * mm});
            skLineSegment(sketch, "E85.4.2", {"start": v(-129.5, 79.35) * mm, "end": v(-129.33, 78.38) * mm});
            skPoint(sketch, "E86.startSnap0", {"position": v(-137.1, 79.68) * mm});
            skLineSegment(sketch, "E87", {"start": v(-136.41, 79.02) * mm, "end": v(-136.56, 78.7) * mm});
            skLineSegment(sketch, "E88", {"start": v(-136.56, 78.7) * mm, "end": v(-140, 82.03) * mm});
            skLineSegment(sketch, "E89", {"start": v(-140, 82.03) * mm, "end": v(-135.27, 81.36) * mm});
            skLineSegment(sketch, "E90", {"start": v(-135.27, 81.36) * mm, "end": v(-135.42, 81.05) * mm});
            skLineSegment(sketch, "E91.1.0", {"start": v(-138.27, 72.17) * mm, "end": v(-136.17, 76.47) * mm});
            skLineSegment(sketch, "E91.1.1", {"start": v(-136.17, 76.47) * mm, "end": v(-135.92, 76.23) * mm});
            skLineSegment(sketch, "E91.1.2", {"start": v(-134.04, 74.42) * mm, "end": v(-138.27, 72.17) * mm});
            skLineSegment(sketch, "E91.1.3", {"start": v(-134.3, 74.66) * mm, "end": v(-134.04, 74.42) * mm});
            skLineSegment(sketch, "E91.2.0", {"start": v(-128.36, 70.78) * mm, "end": v(-131.8, 74.1) * mm});
            skLineSegment(sketch, "E91.2.1", {"start": v(-131.8, 74.1) * mm, "end": v(-131.5, 74.27) * mm});
            skLineSegment(sketch, "E91.2.2", {"start": v(-129.19, 75.5) * mm, "end": v(-128.36, 70.78) * mm});
            skLineSegment(sketch, "E91.2.3", {"start": v(-129.5, 75.33) * mm, "end": v(-129.19, 75.5) * mm});
            skLineSegment(sketch, "E91.3.0", {"start": v(-123.97, 79.78) * mm, "end": v(-128.2, 77.53) * mm});
            skLineSegment(sketch, "E91.3.1", {"start": v(-128.2, 77.53) * mm, "end": v(-128.25, 77.87) * mm});
            skLineSegment(sketch, "E91.3.2", {"start": v(-128.7, 80.44) * mm, "end": v(-123.97, 79.78) * mm});
            skLineSegment(sketch, "E91.3.3", {"start": v(-128.65, 80.1) * mm, "end": v(-128.7, 80.44) * mm});
            skLineSegment(sketch, "E91.4.0", {"start": v(-131.17, 86.73) * mm, "end": v(-130.34, 82.02) * mm});
            skLineSegment(sketch, "E91.4.1", {"start": v(-130.34, 82.02) * mm, "end": v(-130.68, 82.07) * mm});
            skLineSegment(sketch, "E91.4.2", {"start": v(-133.27, 82.43) * mm, "end": v(-131.17, 86.73) * mm});
            skLineSegment(sketch, "E91.4.3", {"start": v(-132.92, 82.38) * mm, "end": v(-133.27, 82.43) * mm});
            skArc(sketch, "E92", {"start": v(-132.28, 78.53) * mm, "mid": v(-132.62, 78.27) * mm, "end": v(-132.37, 77.92) * mm});
            skArc(sketch, "E93", {"start": v(-132.37, 77.92) * mm, "mid": v(-131.74, 78.35) * mm, "end": v(-132.06, 79.04) * mm});
            skArc(sketch, "E94", {"start": v(-132.06, 79.04) * mm, "mid": v(-133.1, 78.5) * mm, "end": v(-132.54, 77.46) * mm});
            skArc(sketch, "E95", {"start": v(-132.28, 78.44) * mm, "mid": v(-132.23, 78.48) * mm, "end": v(-132.28, 78.53) * mm});
            skArc(sketch, "E96", {"start": v(-132.28, 78.44) * mm, "mid": v(-132.53, 78.22) * mm, "end": v(-132.31, 77.97) * mm});
            skArc(sketch, "E97", {"start": v(-132.31, 77.97) * mm, "mid": v(-131.8, 78.43) * mm, "end": v(-132.2, 79) * mm});
            skArc(sketch, "E98", {"start": v(-132.2, 79) * mm, "mid": v(-133.04, 78.38) * mm, "end": v(-132.54, 77.46) * mm});
            skArc(sketch, "E99", {"start": v(-71.26, 14.2) * mm, "mid": v(-72.24, 14.35) * mm, "end": v(-72.1, 13.37) * mm});
            skArc(sketch, "E100", {"start": v(-72.1, 13.37) * mm, "mid": v(-70.03, 13.14) * mm, "end": v(-69.2, 15.05) * mm});
            skArc(sketch, "E101", {"start": v(-69.2, 15.05) * mm, "mid": v(-69.97, 16.61) * mm, "end": v(-71.71, 16.7) * mm});
            skArc(sketch, "E102", {"start": v(-71.26, 14.2) * mm, "mid": v(-70.38, 14.18) * mm, "end": v(-70.53, 15.06) * mm});
            skArc(sketch, "E103", {"start": v(-70.53, 15.06) * mm, "mid": v(-72.93, 15) * mm, "end": v(-72.9, 12.6) * mm});
            skArc(sketch, "E104", {"start": v(-72.9, 12.6) * mm, "mid": v(-69.7, 11.76) * mm, "end": v(-67.17, 13.88) * mm});
            skArc(sketch, "E105", {"start": v(-67.17, 13.88) * mm, "mid": v(-66.27, 16.39) * mm, "end": v(-66.77, 19) * mm});
            skArc(sketch, "E106", {"start": v(-66.77, 19) * mm, "mid": v(-69.76, 18.96) * mm, "end": v(-71.71, 16.7) * mm});
            skArc(sketch, "E107", {"start": v(-68.13, 15.94) * mm, "mid": v(-68.63, 17.13) * mm, "end": v(-69.8, 17.66) * mm});
            skArc(sketch, "E108", {"start": v(-68.13, 15.94) * mm, "mid": v(-67.41, 17.11) * mm, "end": v(-67.56, 18.49) * mm});
            skArc(sketch, "E109", {"start": v(-67.56, 18.49) * mm, "mid": v(-68.8, 18.4) * mm, "end": v(-69.8, 17.66) * mm});
            skArc(sketch, "E110.1.0", {"start": v(-73.98, 7.96) * mm, "mid": v(-72.44, 5.4) * mm, "end": v(-69.5, 4.83) * mm});
            skArc(sketch, "E110.1.1", {"start": v(-69.34, 10.17) * mm, "mid": v(-71.96, 9.7) * mm, "end": v(-73.98, 7.96) * mm});
            skArc(sketch, "E110.1.2", {"start": v(-73.13, 7.53) * mm, "mid": v(-72.43, 6.5) * mm, "end": v(-71.3, 6) * mm});
            skArc(sketch, "E110.1.3", {"start": v(-68.68, 6.67) * mm, "mid": v(-67.43, 4.62) * mm, "end": v(-65.36, 5.85) * mm});
            skArc(sketch, "E110.1.4", {"start": v(-67.58, 6.46) * mm, "mid": v(-67.2, 5.55) * mm, "end": v(-66.43, 6.16) * mm});
            skArc(sketch, "E110.1.5", {"start": v(-70.64, 8.31) * mm, "mid": v(-72.02, 8.35) * mm, "end": v(-73.13, 7.53) * mm});
            skArc(sketch, "E110.1.6", {"start": v(-67.58, 6.46) * mm, "mid": v(-68, 7.24) * mm, "end": v(-68.68, 6.67) * mm});
            skArc(sketch, "E110.1.7", {"start": v(-66.43, 6.16) * mm, "mid": v(-67.27, 8.07) * mm, "end": v(-69.34, 7.83) * mm});
            skArc(sketch, "E110.1.8", {"start": v(-65.36, 5.85) * mm, "mid": v(-66.23, 9.04) * mm, "end": v(-69.34, 10.17) * mm});
            skArc(sketch, "E110.1.9", {"start": v(-70.64, 8.31) * mm, "mid": v(-71.42, 7.29) * mm, "end": v(-71.3, 6) * mm});
            skArc(sketch, "E110.1.10", {"start": v(-69.34, 7.83) * mm, "mid": v(-70.3, 6.38) * mm, "end": v(-69.5, 4.83) * mm});
            skArc(sketch, "E110.2.0", {"start": v(-60.8, 7.24) * mm, "mid": v(-59.35, 9.85) * mm, "end": v(-60.34, 12.68) * mm});
            skArc(sketch, "E110.2.1", {"start": v(-65.04, 10.15) * mm, "mid": v(-63.32, 8.11) * mm, "end": v(-60.8, 7.24) * mm});
            skArc(sketch, "E110.2.2", {"start": v(-60.86, 8.18) * mm, "mid": v(-60.32, 9.3) * mm, "end": v(-60.45, 10.54) * mm});
            skArc(sketch, "E110.2.3", {"start": v(-62.34, 12.47) * mm, "mid": v(-61.2, 14.58) * mm, "end": v(-63.29, 15.75) * mm});
            skArc(sketch, "E110.2.4", {"start": v(-62.71, 13.53) * mm, "mid": v(-62.1, 14.3) * mm, "end": v(-63.02, 14.67) * mm});
            skArc(sketch, "E110.2.5", {"start": v(-62.78, 9.95) * mm, "mid": v(-62.12, 8.74) * mm, "end": v(-60.86, 8.18) * mm});
            skArc(sketch, "E110.2.6", {"start": v(-62.71, 13.53) * mm, "mid": v(-63.18, 12.77) * mm, "end": v(-62.34, 12.47) * mm});
            skArc(sketch, "E110.2.7", {"start": v(-63.02, 14.67) * mm, "mid": v(-64.26, 13) * mm, "end": v(-63.02, 11.32) * mm});
            skArc(sketch, "E110.2.8", {"start": v(-63.29, 15.75) * mm, "mid": v(-65.62, 13.4) * mm, "end": v(-65.04, 10.15) * mm});
            skArc(sketch, "E110.2.9", {"start": v(-62.78, 9.95) * mm, "mid": v(-61.5, 9.79) * mm, "end": v(-60.45, 10.54) * mm});
            skArc(sketch, "E110.2.10", {"start": v(-63.02, 11.32) * mm, "mid": v(-61.28, 11.2) * mm, "end": v(-60.34, 12.68) * mm});
            skPoint(sketch, "E110.center", {"position": v(-67.18, 11.4) * mm});
            skArc(sketch, "E111", {"start": v(-67.03, 11.52) * mm, "mid": v(-67.38, 11.52) * mm, "end": v(-67.4, 11.17) * mm});
            skArc(sketch, "E112", {"start": v(-67.4, 11.17) * mm, "mid": v(-66.62, 11.23) * mm, "end": v(-66.76, 12) * mm});
            skArc(sketch, "E113", {"start": v(-66.76, 12) * mm, "mid": v(-67.89, 11.7) * mm, "end": v(-67.55, 10.59) * mm});
            skArc(sketch, "E114", {"start": v(-67.08, 11.43) * mm, "mid": v(-67.02, 11.45) * mm, "end": v(-67.03, 11.52) * mm});
            skArc(sketch, "E115", {"start": v(-67.08, 11.43) * mm, "mid": v(-67.34, 11.33) * mm, "end": v(-67.16, 11.1) * mm});
            skArc(sketch, "E116", {"start": v(-67.16, 11.1) * mm, "mid": v(-66.72, 11.23) * mm, "end": v(-66.58, 11.68) * mm});
            skArc(sketch, "E117", {"start": v(-66.58, 11.68) * mm, "mid": v(-66.96, 12.03) * mm, "end": v(-67.48, 11.96) * mm});
            skArc(sketch, "E118", {"start": v(-67.48, 11.96) * mm, "mid": v(-67.79, 11.69) * mm, "end": v(-67.88, 11.28) * mm});
            skArc(sketch, "E119", {"start": v(-67.88, 11.28) * mm, "mid": v(-67.8, 10.9) * mm, "end": v(-67.55, 10.59) * mm});
            skArc(sketch, "E120", {"start": v(-112.33, -70.34) * mm, "mid": v(-115.3, -71.4) * mm, "end": v(-117.45, -73.7) * mm});
            skArc(sketch, "E121", {"start": v(-117.45, -73.7) * mm, "mid": v(-114.34, -74.03) * mm, "end": v(-111.36, -73.05) * mm});
            skArc(sketch, "E122", {"start": v(-105, -76.12) * mm, "mid": v(-106.28, -73.08) * mm, "end": v(-108.73, -70.88) * mm});
            skArc(sketch, "E123", {"start": v(-110.72, -73.21) * mm, "mid": v(-108.24, -75.4) * mm, "end": v(-105, -76.12) * mm});
            skArc(sketch, "E124", {"start": v(-108.73, -70.88) * mm, "mid": v(-110.48, -70.33) * mm, "end": v(-112.33, -70.34) * mm});
            skArc(sketch, "E125", {"start": v(-108.88, -70.34) * mm, "mid": v(-108.35, -67.17) * mm, "end": v(-109.3, -64.09) * mm});
            skArc(sketch, "E126", {"start": v(-111.36, -73.05) * mm, "mid": v(-109.88, -71.92) * mm, "end": v(-108.88, -70.34) * mm});
            skArc(sketch, "E127", {"start": v(-109.3, -64.09) * mm, "mid": v(-111.32, -66.58) * mm, "end": v(-111.83, -69.75) * mm});
            skArc(sketch, "E128", {"start": v(-111.83, -69.75) * mm, "mid": v(-111.5, -71.55) * mm, "end": v(-110.72, -73.21) * mm});
            skLineSegment(sketch, "E129", {"start": v(-143.9, 17.62) * mm, "end": v(-146.3, 3.98) * mm});
            skLineSegment(sketch, "E130", {"start": v(-146.3, 3.98) * mm, "end": v(-159.94, 6.38) * mm});
            skLineSegment(sketch, "E131", {"start": v(-159.94, 6.38) * mm, "end": v(-159.53, 8.7) * mm});
            skLineSegment(sketch, "E132", {"start": v(-159.53, 8.7) * mm, "end": v(-170, 7.09) * mm});
            skLineSegment(sketch, "E133", {"start": v(-170, 7.09) * mm, "end": v(-160.79, 1.57) * mm});
            skLineSegment(sketch, "E134", {"start": v(-160.79, 1.57) * mm, "end": v(-160.38, 3.88) * mm});
            skLineSegment(sketch, "E135", {"start": v(-160.38, 3.88) * mm, "end": v(-146.74, 1.48) * mm});
            skLineSegment(sketch, "E136", {"start": v(-146.74, 1.48) * mm, "end": v(-149.14, -12.16) * mm});
            skLineSegment(sketch, "E137.1.0", {"start": v(-120.9, -2) * mm, "end": v(-130.12, 3.5) * mm});
            skLineSegment(sketch, "E137.1.1", {"start": v(-131.37, -3.62) * mm, "end": v(-120.9, -2) * mm});
            skLineSegment(sketch, "E137.1.2", {"start": v(-147.01, -12.54) * mm, "end": v(-144.6, 1.1) * mm});
            skLineSegment(sketch, "E137.1.3", {"start": v(-130.53, 1.2) * mm, "end": v(-144.16, 3.6) * mm});
            skLineSegment(sketch, "E137.1.4", {"start": v(-144.6, 1.1) * mm, "end": v(-130.97, -1.3) * mm});
            skLineSegment(sketch, "E137.1.5", {"start": v(-144.16, 3.6) * mm, "end": v(-141.76, 17.24) * mm});
            skLineSegment(sketch, "E137.1.6", {"start": v(-130.12, 3.5) * mm, "end": v(-130.53, 1.2) * mm});
            skLineSegment(sketch, "E137.1.7", {"start": v(-130.97, -1.3) * mm, "end": v(-131.37, -3.62) * mm});
            skPoint(sketch, "E137.center", {"position": v(-145.45, 2.54) * mm});
            skLineSegment(sketch, "E138.1.0", {"start": v(-139.43, 16.92) * mm, "end": v(-141.06, 27.36) * mm});
            skLineSegment(sketch, "E138.1.1", {"start": v(-141.76, 17.24) * mm, "end": v(-139.43, 16.92) * mm});
            skLineSegment(sketch, "E138.1.2", {"start": v(-141.06, 27.36) * mm, "end": v(-146.22, 17.94) * mm});
            skLineSegment(sketch, "E138.1.3", {"start": v(-146.22, 17.94) * mm, "end": v(-143.9, 17.62) * mm});
            skLineSegment(sketch, "E138.2.0", {"start": v(-151.46, -11.75) * mm, "end": v(-149.85, -22.23) * mm});
            skLineSegment(sketch, "E138.2.1", {"start": v(-149.14, -12.16) * mm, "end": v(-151.46, -11.75) * mm});
            skLineSegment(sketch, "E138.2.2", {"start": v(-149.85, -22.23) * mm, "end": v(-144.7, -12.95) * mm});
            skLineSegment(sketch, "E138.2.3", {"start": v(-144.7, -12.95) * mm, "end": v(-147.01, -12.54) * mm});
            skLineSegment(sketch, "E139.0", {"start": v(-146.74, 1.48) * mm, "end": v(-146.74, 1.48) * mm});
            skLineSegment(sketch, "E139.1", {"start": v(-146.74, 1.48) * mm, "end": v(-146.3, 3.98) * mm, "construction": true});
            skLineSegment(sketch, "E140.0", {"start": v(-143.9, 17.62) * mm, "end": v(-141.76, 17.24) * mm, "construction": true});
            skLineSegment(sketch, "E141.0", {"start": v(-160.38, 3.88) * mm, "end": v(-159.94, 6.38) * mm, "construction": true});
            skSolve(sketch);
        }
        {
            var Q0;
            Q0=makeQuery(id+"F3.imprint","IMPRINT",FACE,{"disambiguationData":[TD([[makeQuery(id+"F3.imprint","IMPRINT",EDGE,{"derivedFrom":sQuery(id+"F3.wireOp",EDGE,"E22")}),1.0]])]});
            var Q1;
            Q1=makeQuery(id+"F3.imprint","IMPRINT",FACE,{"disambiguationData":[TD([[makeQuery(id+"F3.imprint","IMPRINT",EDGE,{"derivedFrom":sQuery(id+"F3.wireOp",EDGE,"E23")}),1.0]])]});
            var Q2;
            Q2=makeQuery(id+"F3.imprint","IMPRINT",FACE,{"disambiguationData":[TD([[makeQuery(id+"F3.imprint","IMPRINT",EDGE,{"derivedFrom":sQuery(id+"F3.wireOp",EDGE,"E24")}),1.0]])]});
            var Q3;
            Q3=makeQuery(id+"F3.imprint","IMPRINT",FACE,{"disambiguationData":[TD([[makeQuery(id+"F3.imprint","IMPRINT",EDGE,{"derivedFrom":sQuery(id+"F3.wireOp",EDGE,"E41")}),1.0]])]});
            var Q4;
            Q4=makeQuery(id+"F3.imprint","IMPRINT",FACE,{"disambiguationData":[TD([[makeQuery(id+"F3.imprint","IMPRINT",EDGE,{"derivedFrom":sQuery(id+"F3.wireOp",EDGE,"E45.1.0")}),1.0]])]});
            var Q5;
            Q5=makeQuery(id+"F3.imprint","IMPRINT",FACE,{"disambiguationData":[TD([[makeQuery(id+"F3.imprint","IMPRINT",EDGE,{"derivedFrom":sQuery(id+"F3.wireOp",EDGE,"E45.2.0")}),1.0]])]});
            var Q6;
            Q6=makeQuery(id+"F3.imprint","IMPRINT",FACE,{"disambiguationData":[TD([[makeQuery(id+"F3.imprint","IMPRINT",EDGE,{"derivedFrom":sQuery(id+"F3.wireOp",EDGE,"E45.3.0")}),1.0]])]});
            var Q7;
            Q7=makeQuery(id+"F3.imprint","IMPRINT",FACE,{"disambiguationData":[TD([[makeQuery(id+"F3.imprint","IMPRINT",EDGE,{"derivedFrom":sQuery(id+"F3.wireOp",EDGE,"E111")}),1.0]])]});
            var Q8;
            {var subQ1=sQuery(id+"F3.wireOp",EDGE,"E26");Q8=makeQuery(id+"F3.imprint","IMPRINT",FACE,{"disambiguationData":[TD([[makeQuery(id+"F3.imprint","IMPRINT",EDGE,{"derivedFrom":subQ1}),1.0]])]});}
            var Q9;
            {var subQ0=sQuery(id+"F3.wireOp",EDGE,"E29");var subQ1=makeQuery(id+"F3.imprint","INTERSECT",VERTEX,{"derivedFrom":[sQuery(id+"F3.wireOp",EDGE,"E26"),subQ0]});Q9=makeQuery(id+"F3.imprint","IMPRINT",FACE,{"disambiguationData":[TD([[makeQuery(id+"F3.imprint","IMPRINT",EDGE,{"disambiguationData":[TD([[subQ1,1.0]])],"derivedFrom":subQ0}),1.0]])]});}
            var Q10;
            {var subQ0=sQuery(id+"F3.wireOp",EDGE,"E31.1.0");var subQ1=makeQuery(id+"F3.imprint","INTERSECT",VERTEX,{"derivedFrom":[subQ0,sQuery(id+"F3.wireOp",EDGE,"E31.1.1")]});Q10=makeQuery(id+"F3.imprint","IMPRINT",FACE,{"disambiguationData":[TD([[makeQuery(id+"F3.imprint","IMPRINT",EDGE,{"disambiguationData":[TD([[subQ1,-1.0]])],"derivedFrom":subQ0}),1.0]])]});}
            var Q11;
            {var subQ1=sQuery(id+"F3.wireOp",EDGE,"E31.1.1");Q11=makeQuery(id+"F3.imprint","IMPRINT",FACE,{"disambiguationData":[TD([[makeQuery(id+"F3.imprint","IMPRINT",EDGE,{"derivedFrom":subQ1}),-1.0]])]});}
            var Q12;
            {var subQ0=sQuery(id+"F3.wireOp",EDGE,"E31.2.0");var subQ1=makeQuery(id+"F3.imprint","INTERSECT",VERTEX,{"derivedFrom":[subQ0,sQuery(id+"F3.wireOp",EDGE,"E31.2.1")]});Q12=makeQuery(id+"F3.imprint","IMPRINT",FACE,{"disambiguationData":[TD([[makeQuery(id+"F3.imprint","IMPRINT",EDGE,{"disambiguationData":[TD([[subQ1,-1.0]])],"derivedFrom":subQ0}),1.0]])]});}
            var Q13;
            {var subQ1=sQuery(id+"F3.wireOp",EDGE,"E31.2.1");Q13=makeQuery(id+"F3.imprint","IMPRINT",FACE,{"disambiguationData":[TD([[makeQuery(id+"F3.imprint","IMPRINT",EDGE,{"derivedFrom":subQ1}),-1.0]])]});}
            var Q14;
            Q14=makeQuery(id+"F3.imprint","IMPRINT",FACE,{"disambiguationData":[TD([[makeQuery(id+"F3.imprint","IMPRINT",EDGE,{"derivedFrom":sQuery(id+"F3.wireOp",EDGE,"E63")}),1.0]])]});
            var Q15;
            Q15=makeQuery(id+"F3.imprint","IMPRINT",FACE,{"disambiguationData":[TD([[makeQuery(id+"F3.imprint","IMPRINT",EDGE,{"derivedFrom":sQuery(id+"F3.wireOp",EDGE,"E67.1.0")}),1.0]])]});
            var Q16;
            Q16=makeQuery(id+"F3.imprint","IMPRINT",FACE,{"disambiguationData":[TD([[makeQuery(id+"F3.imprint","IMPRINT",EDGE,{"derivedFrom":sQuery(id+"F3.wireOp",EDGE,"E67.2.0")}),1.0]])]});
            var Q17;
            Q17=makeQuery(id+"F3.imprint","IMPRINT",FACE,{"disambiguationData":[TD([[makeQuery(id+"F3.imprint","IMPRINT",EDGE,{"derivedFrom":sQuery(id+"F3.wireOp",EDGE,"E99")}),-1.0]])]});
            var Q18;
            Q18=makeQuery(id+"F3.imprint","IMPRINT",FACE,{"disambiguationData":[TD([[makeQuery(id+"F3.imprint","IMPRINT",EDGE,{"derivedFrom":sQuery(id+"F3.wireOp",EDGE,"E110.1.0")}),1.0]])]});
            var Q19;
            Q19=makeQuery(id+"F3.imprint","IMPRINT",FACE,{"disambiguationData":[TD([[makeQuery(id+"F3.imprint","IMPRINT",EDGE,{"derivedFrom":sQuery(id+"F3.wireOp",EDGE,"E110.2.0")}),1.0]])]});
            var Q20;
            {var subQ1=sQuery(id+"F3.wireOp",EDGE,"E34");Q20=makeQuery(id+"F3.imprint","IMPRINT",FACE,{"disambiguationData":[TD([[makeQuery(id+"F3.imprint","IMPRINT",EDGE,{"derivedFrom":subQ1}),-1.0]])]});}
            var Q21;
            Q21=makeQuery(id+"F3.imprint","IMPRINT",FACE,{"disambiguationData":[TD([[makeQuery(id+"F3.imprint","IMPRINT",EDGE,{"derivedFrom":sQuery(id+"F3.wireOp",EDGE,"E40.2.1")}),1.0]])]});
            var Q22;
            {var subQ0=sQuery(id+"F3.wireOp",EDGE,"E122");Q22=makeQuery(id+"F3.imprint","IMPRINT",FACE,{"disambiguationData":[TD([[makeQuery(id+"F3.imprint","IMPRINT",EDGE,{"derivedFrom":subQ0}),-1.0]])]});}
            var Q23;
            {var subQ7=sQuery(id+"F3.wireOp",EDGE,"E125");Q23=makeQuery(id+"F3.imprint","IMPRINT",FACE,{"disambiguationData":[TD([[makeQuery(id+"F3.imprint","IMPRINT",EDGE,{"derivedFrom":subQ7}),-1.0]])]});}
            var Q24;
            {var subQ1=sQuery(id+"F3.wireOp",EDGE,"E50");var subQ3=sQuery(id+"F3.wireOp",EDGE,"E51.2.0");var subQ4=makeQuery(id+"F3.imprint","INTERSECT",VERTEX,{"disambiguationData":[OD(1.0)],"derivedFrom":[subQ1,subQ3]});Q24=makeQuery(id+"F3.imprint","IMPRINT",FACE,{"disambiguationData":[TD([[makeQuery(id+"F3.imprint","IMPRINT",EDGE,{"disambiguationData":[TD([[subQ4,-1.0]])],"derivedFrom":subQ1}),1.0]])]});}
            var Q25;
            {var subQ1=sQuery(id+"F3.wireOp",EDGE,"E50");var subQ3=sQuery(id+"F3.wireOp",EDGE,"E51.1.0");var subQ4=makeQuery(id+"F3.imprint","INTERSECT",VERTEX,{"disambiguationData":[OD(1.0)],"derivedFrom":[subQ1,subQ3]});Q25=makeQuery(id+"F3.imprint","IMPRINT",FACE,{"disambiguationData":[TD([[makeQuery(id+"F3.imprint","IMPRINT",EDGE,{"disambiguationData":[TD([[subQ4,1.0]])],"derivedFrom":subQ1}),1.0]])]});}
            var Q26;
            {var subQ6=sQuery(id+"F3.wireOp",EDGE,"E120");Q26=makeQuery(id+"F3.imprint","IMPRINT",FACE,{"disambiguationData":[TD([[makeQuery(id+"F3.imprint","IMPRINT",EDGE,{"derivedFrom":subQ6}),-1.0]])]});}
            var Q27;
            {var subQ1=sQuery(id+"F3.wireOp",EDGE,"E51.1.0");var subQ3=sQuery(id+"F3.wireOp",EDGE,"E51.2.0");var subQ4=makeQuery(id+"F3.imprint","INTERSECT",VERTEX,{"disambiguationData":[OD(1.0)],"derivedFrom":[subQ1,subQ3]});Q27=makeQuery(id+"F3.imprint","IMPRINT",FACE,{"disambiguationData":[TD([[makeQuery(id+"F3.imprint","IMPRINT",EDGE,{"disambiguationData":[TD([[subQ4,1.0]])],"derivedFrom":subQ1}),1.0]])]});}
            var Q28;
            Q28=makeQuery(id+"F3.imprint","IMPRINT",FACE,{"disambiguationData":[TD([[makeQuery(id+"F3.imprint","IMPRINT",EDGE,{"derivedFrom":sQuery(id+"F3.wireOp",EDGE,"E40.1.1")}),1.0]])]});
            var Q29;
            {var subQ0=sQuery(id+"F3.wireOp",EDGE,"E124");var subQ5=sQuery(id+"F3.wireOp",EDGE,"E126");var subQ6=makeQuery(id+"F3.imprint","INTERSECT",VERTEX,{"derivedFrom":[subQ0,subQ5]});Q29=makeQuery(id+"F3.imprint","IMPRINT",FACE,{"disambiguationData":[TD([[makeQuery(id+"F3.imprint","IMPRINT",EDGE,{"disambiguationData":[TD([[subQ6,1.0]])],"derivedFrom":subQ5}),-1.0]])]});}
            var Q30;
            {var subQ0=sQuery(id+"F3.wireOp",EDGE,"E126");var subQ5=sQuery(id+"F3.wireOp",EDGE,"E124");var subQ6=makeQuery(id+"F3.imprint","INTERSECT",VERTEX,{"derivedFrom":[subQ5,subQ0]});Q30=makeQuery(id+"F3.imprint","IMPRINT",FACE,{"disambiguationData":[TD([[makeQuery(id+"F3.imprint","IMPRINT",EDGE,{"disambiguationData":[TD([[subQ6,-1.0]])],"derivedFrom":subQ5}),-1.0]])]});}
            var Q31;
            {var subQ0=sQuery(id+"F3.wireOp",EDGE,"E124");var subQ5=sQuery(id+"F3.wireOp",EDGE,"E128");var subQ6=makeQuery(id+"F3.imprint","INTERSECT",VERTEX,{"derivedFrom":[subQ0,subQ5]});Q31=makeQuery(id+"F3.imprint","IMPRINT",FACE,{"disambiguationData":[TD([[makeQuery(id+"F3.imprint","IMPRINT",EDGE,{"disambiguationData":[TD([[subQ6,-1.0]])],"derivedFrom":subQ5}),-1.0]])]});}
            var Q32;
            {var subQ5=sQuery(id+"F3.wireOp",EDGE,"E68.0");Q32=makeQuery(id+"F3.imprint","IMPRINT",FACE,{"disambiguationData":[TD([[makeQuery(id+"F3.imprint","IMPRINT",EDGE,{"derivedFrom":subQ5}),1.0]])]});}
            var Q33;
            Q33=makeQuery(id+"F3.imprint","IMPRINT",FACE,{"disambiguationData":[TD([[makeQuery(id+"F3.imprint","IMPRINT",EDGE,{"derivedFrom":sQuery(id+"F3.wireOp",EDGE,"E68.0")}),-1.0]])]});
            var Q34;
            {var subQ5=sQuery(id+"F3.wireOp",EDGE,"E68.3");Q34=makeQuery(id+"F3.imprint","IMPRINT",FACE,{"disambiguationData":[TD([[makeQuery(id+"F3.imprint","IMPRINT",EDGE,{"derivedFrom":subQ5}),1.0]])]});}
            var Q35;
            {var subQ5=sQuery(id+"F3.wireOp",EDGE,"E68.4");Q35=makeQuery(id+"F3.imprint","IMPRINT",FACE,{"disambiguationData":[TD([[makeQuery(id+"F3.imprint","IMPRINT",EDGE,{"derivedFrom":subQ5}),1.0]])]});}
            var Q36;
            {var subQ5=sQuery(id+"F3.wireOp",EDGE,"E68.2");Q36=makeQuery(id+"F3.imprint","IMPRINT",FACE,{"disambiguationData":[TD([[makeQuery(id+"F3.imprint","IMPRINT",EDGE,{"derivedFrom":subQ5}),1.0]])]});}
            var Q37;
            {var subQ5=sQuery(id+"F3.wireOp",EDGE,"E68.1");Q37=makeQuery(id+"F3.imprint","IMPRINT",FACE,{"disambiguationData":[TD([[makeQuery(id+"F3.imprint","IMPRINT",EDGE,{"derivedFrom":subQ5}),1.0]])]});}
            extrude(context, id + "F4", {"entities" : qUnion([Q0, Q1, Q2, Q3, Q4, Q5, Q6, Q7, Q8, Q9, Q10, Q11, Q12, Q13, Q14, Q15, Q16, Q17, Q18, Q19, Q20, Q21, Q22, Q23, Q24, Q25, Q26, Q27, Q28, Q29, Q30, Q31, Q32, Q33, Q34, Q35, Q36, Q37]), "operationType" : NewBodyOperationType.REMOVE, "oppositeDirection" : true, "depth" : 1.27 * mm, "offsetDistance" : 25.4 * mm});
        }
        {
            var Q0;
            Q0=makeQuery(id+"F3.imprint","IMPRINT",FACE,{"disambiguationData":[TD([[makeQuery(id+"F3.imprint","IMPRINT",EDGE,{"derivedFrom":sQuery(id+"F3.wireOp",EDGE,"E91.3.0")}),-1.0]])]});
            var Q1;
            Q1=makeQuery(id+"F3.imprint","IMPRINT",FACE,{"disambiguationData":[TD([[makeQuery(id+"F3.imprint","IMPRINT",EDGE,{"derivedFrom":sQuery(id+"F3.wireOp",EDGE,"E91.2.0")}),-1.0]])]});
            var Q2;
            Q2=makeQuery(id+"F3.imprint","IMPRINT",FACE,{"disambiguationData":[TD([[makeQuery(id+"F3.imprint","IMPRINT",EDGE,{"derivedFrom":sQuery(id+"F3.wireOp",EDGE,"E91.1.0")}),-1.0]])]});
            var Q3;
            {var subQ0=sQuery(id+"F3.wireOp",EDGE,"E87");Q3=makeQuery(id+"F3.imprint","IMPRINT",FACE,{"disambiguationData":[TD([[makeQuery(id+"F3.imprint","IMPRINT",EDGE,{"derivedFrom":subQ0}),-1.0]])]});}
            var Q4;
            Q4=makeQuery(id+"F3.imprint","IMPRINT",FACE,{"disambiguationData":[TD([[makeQuery(id+"F3.imprint","IMPRINT",EDGE,{"derivedFrom":sQuery(id+"F3.wireOp",EDGE,"E91.4.0")}),-1.0]])]});
            var Q5;
            Q5=makeQuery(id+"F3.imprint","IMPRINT",FACE,{"disambiguationData":[TD([[makeQuery(id+"F3.imprint","IMPRINT",EDGE,{"derivedFrom":sQuery(id+"F3.wireOp",EDGE,"E69")}),1.0]])]});
            var Q6;
            {var subQ0=sQuery(id+"F3.wireOp",EDGE,"E47");var subQ1=sQuery(id+"F3.wireOp",EDGE,"E32");var subQ2=makeQuery(id+"F3.imprint","INTERSECT",VERTEX,{"derivedFrom":[subQ1,subQ0]});Q6=makeQuery(id+"F3.imprint","IMPRINT",FACE,{"disambiguationData":[TD([[makeQuery(id+"F3.imprint","IMPRINT",EDGE,{"disambiguationData":[TD([[subQ2,-1.0]])],"derivedFrom":subQ1}),1.0]])]});}
            var Q7;
            {var subQ0=sQuery(id+"F3.wireOp",EDGE,"E47");var subQ1=sQuery(id+"F3.wireOp",EDGE,"E32");var subQ2=makeQuery(id+"F3.imprint","INTERSECT",VERTEX,{"derivedFrom":[subQ1,subQ0]});Q7=makeQuery(id+"F3.imprint","IMPRINT",FACE,{"disambiguationData":[TD([[makeQuery(id+"F3.imprint","IMPRINT",EDGE,{"disambiguationData":[TD([[subQ2,-1.0]])],"derivedFrom":subQ1}),-1.0]])]});}
            var Q8;
            {var subQ0=sQuery(id+"F3.wireOp",EDGE,"E47");var subQ1=sQuery(id+"F3.wireOp",EDGE,"E33");var subQ2=makeQuery(id+"F3.imprint","INTERSECT",VERTEX,{"derivedFrom":[subQ1,subQ0]});Q8=makeQuery(id+"F3.imprint","IMPRINT",FACE,{"disambiguationData":[TD([[makeQuery(id+"F3.imprint","IMPRINT",EDGE,{"disambiguationData":[TD([[subQ2,-1.0]])],"derivedFrom":subQ1}),1.0]])]});}
            var Q9;
            {var subQ0=sQuery(id+"F3.wireOp",EDGE,"E48");var subQ1=sQuery(id+"F3.wireOp",EDGE,"E40.1.0");var subQ2=makeQuery(id+"F3.imprint","INTERSECT",VERTEX,{"derivedFrom":[subQ1,subQ0]});Q9=makeQuery(id+"F3.imprint","IMPRINT",FACE,{"disambiguationData":[TD([[makeQuery(id+"F3.imprint","IMPRINT",EDGE,{"disambiguationData":[TD([[subQ2,1.0]])],"derivedFrom":subQ1}),-1.0]])]});}
            var Q10;
            {var subQ0=sQuery(id+"F3.wireOp",EDGE,"E49");var subQ1=sQuery(id+"F3.wireOp",EDGE,"E40.2.0");var subQ2=makeQuery(id+"F3.imprint","INTERSECT",VERTEX,{"derivedFrom":[subQ1,subQ0]});Q10=makeQuery(id+"F3.imprint","IMPRINT",FACE,{"disambiguationData":[TD([[makeQuery(id+"F3.imprint","IMPRINT",EDGE,{"disambiguationData":[TD([[subQ2,-1.0]])],"derivedFrom":subQ1}),1.0]])]});}
            var Q11;
            {var subQ0=sQuery(id+"F3.wireOp",EDGE,"E49");var subQ1=sQuery(id+"F3.wireOp",EDGE,"E40.2.0");var subQ2=makeQuery(id+"F3.imprint","INTERSECT",VERTEX,{"derivedFrom":[subQ1,subQ0]});Q11=makeQuery(id+"F3.imprint","IMPRINT",FACE,{"disambiguationData":[TD([[makeQuery(id+"F3.imprint","IMPRINT",EDGE,{"disambiguationData":[TD([[subQ2,-1.0]])],"derivedFrom":subQ1}),-1.0]])]});}
            extrude(context, id + "F5", {"entities" : qUnion([Q0, Q1, Q2, Q3, Q4, Q5, Q6, Q7, Q8, Q9, Q10, Q11]), "operationType" : NewBodyOperationType.ADD, "depth" : 1.27 * mm, "offsetDistance" : 25.4 * mm});
        }
        {
            var Q0;
            Q0=makeQuery(id+"F3.imprint","IMPRINT",FACE,{"disambiguationData":[TD([[makeQuery(id+"F3.imprint","IMPRINT",EDGE,{"derivedFrom":sQuery(id+"F3.wireOp",EDGE,"E129")}),1.0]])]});
            extrude(context, id + "F6", {"entities" : qUnion([Q0]), "operationType" : NewBodyOperationType.REMOVE, "endBound" : BoundingType.THROUGH_ALL, "oppositeDirection" : true, "depth" : 25.4 * mm, "offsetDistance" : 25.4 * mm});
        }
    });
